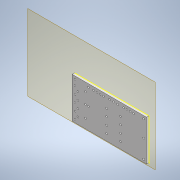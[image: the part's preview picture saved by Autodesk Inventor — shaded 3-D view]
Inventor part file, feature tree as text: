
AUTODESK INVENTOR PART (.ipt)
format: ipt  version: 2021 (Build 250183000, 183)  size: 477,184 bytes
history: native  units: in
note: dims shown in document units (in); Inventor stores cm internally (conversion verified against a paired STEP export)
features: reference x63, projected_geometry x16, other x10, extrude x3, hole x3, sketch x2, plane x1
ambient origin geometry x8: Origin, YZ Plane, XZ Plane, XY Plane, X Axis, Y Axis, Z Axis, Center Point
bodies: Solid1 (feature_tree)
feature tree (98):
  extrude  "Extrusion base plate"  [1 undecoded]
  plane  "work plane for rib creation"
  other  "channels as rib"
  extrude  "extrusion of ribs to get cutout"  Depth=0.2756in
  extrude  "valve space extrusion"  Depth=0.9055in
  other  "all valve spaces"
  other  "projected points for every hole for control layer only"
  hole  "holes for control layer"  [1 undecoded]
  other  "projected points for every hole for flow layer only"
  hole  "holes for connection to flow layer"  [1 undecoded]
  hole  "holes in corners"  [1 undecoded]
  other  "all holes for flow layer only"
  sketch  "Sketch1"  dims[d2=0.2362in d3=0.0in d4=-0.0394in]
  other  "channels and points for valves and for connectors for control layer"
  reference  "Reference1"
  reference  "Reference2"
  reference  "Reference3"
  reference  "Reference4"
  reference  "Reference5"
  reference  "Reference6"
  reference  "Reference7"
  reference  "Reference8"
  reference  "Reference9"
  reference  "Reference10"
  reference  "Reference11"
  reference  "Reference12"
  reference  "Reference13"
  reference  "Reference14"
  reference  "Reference15"
  reference  "Reference16"
  reference  "Reference17"
  reference  "Reference18"
  reference  "Reference19"
  reference  "Reference20"
  reference  "Reference21"
  reference  "Reference22"
  reference  "Reference23"
  reference  "Reference24"
  reference  "Reference25"
  reference  "Reference26"
  reference  "Reference27"
  reference  "Reference28"
  reference  "Reference29"
  reference  "Reference30"
  reference  "Reference31"
  reference  "Reference32"
  reference  "Reference33"
  reference  "Reference34"
  reference  "Reference35"
  sketch  "Sketch3"  dims[d5=7.874in d6=11.811in d7=0.9055in d9=0.3543in d10=0.3543in d11=0.3543in d12=0.3543in d19=0.0394in d20=0.0394in d21=0.0in d22=0.0in d23=0.0394in d24=0.0in d25=0.1024in d26=0.0in d27=0.063in d28=0.0in d29=0.1654in d30=0.2362in d31=0.1575in d32=0.0787in d33=90.0deg d34=0.0394in d35=0.0in d36=0.1654in d37=0.2362in d38=0.1575in d39=0.0787in d40=90.0deg d41=0.0394in d42=0.0in d43=0.1772in d44=0.2362in d45=0.1575in d46=0.0787in d47=90.0deg d48=0.315in d49=0.8108in d50=0.1181in d51=0.0886in d52=0.2756in]
  projected_geometry  "Projected Loop1"
  projected_geometry  "Projected Loop2"
  projected_geometry  "Projected Loop3"
  projected_geometry  "Projected Loop4"
  projected_geometry  "Projected Loop5"
  projected_geometry  "Projected Loop6"
  projected_geometry  "Projected Loop7"
  projected_geometry  "Projected Loop8"
  projected_geometry  "Projected Loop9"
  projected_geometry  "Projected Loop10"
  projected_geometry  "Projected Loop11"
  projected_geometry  "Projected Loop12"
  projected_geometry  "Projected Loop13"
  projected_geometry  "Projected Loop14"
  projected_geometry  "Projected Loop15"
  projected_geometry  "Projected Loop16"
  reference  "Reference36"
  other  "Projected points for every valve"
  reference  "Reference37"
  reference  "Reference38"
  reference  "Reference39"
  reference  "Reference40"
  reference  "Reference41"
  reference  "Reference42"
  reference  "Reference43"
  reference  "Reference44"
  reference  "Reference45"
  reference  "Reference46"
  reference  "Reference47"
  reference  "Reference48"
  reference  "Reference49"
  reference  "Reference50"
  reference  "Reference51"
  reference  "Reference52"
  reference  "Reference53"
  reference  "Reference54"
  reference  "Reference55"
  reference  "Reference56"
  other  "projection for holes in corners"
  reference  "Reference57"
  reference  "Reference58"
  reference  "Reference59"
  reference  "Reference60"
  reference  "Reference61"
  reference  "Reference62"
  reference  "Reference63"
  other  "Millifluidic Board.iam"
  other  "Flow Layer:1"
note: 4 required parameter values undecoded (feature->parameter linkage not recoverable at this tier; creation-order binding heuristic only, values carry confidence <= 0.55)
